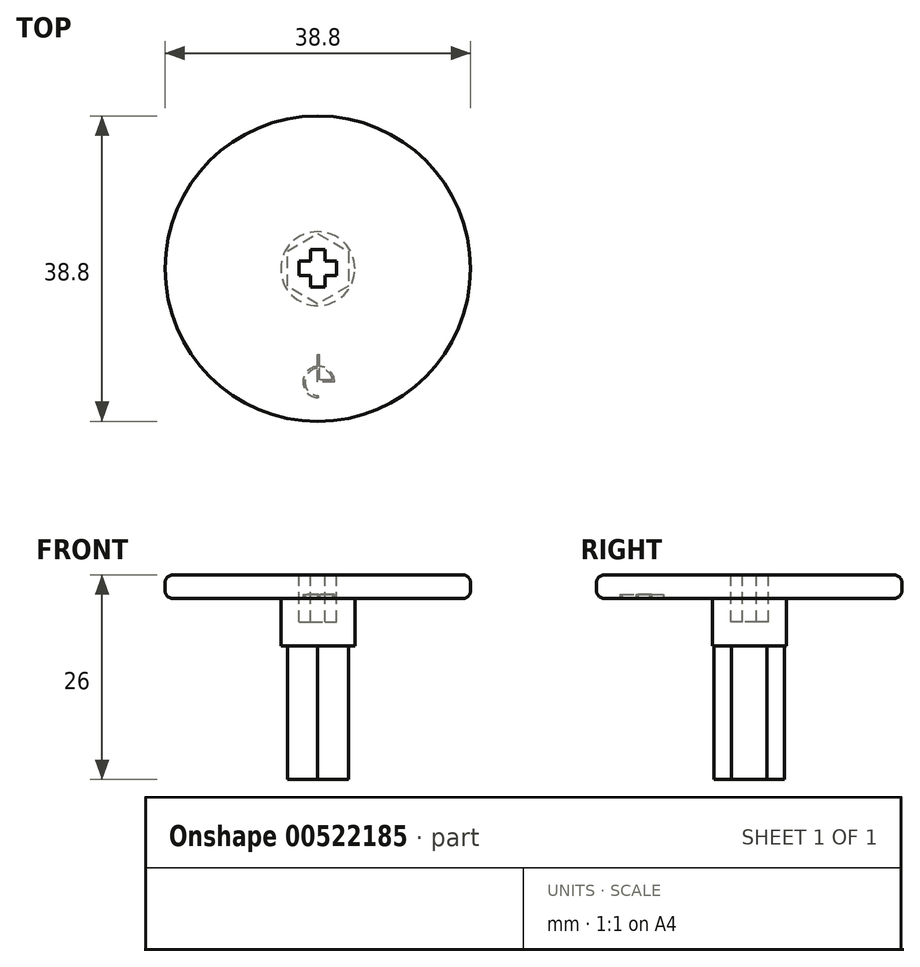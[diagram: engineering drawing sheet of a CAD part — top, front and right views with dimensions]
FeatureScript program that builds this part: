
annotation { "Feature Type Name" : "Feature", "Feature Type Description" : "" }
export const myFeature = defineFeature(function(context is Context, id is Id, definition is map)
    precondition{}
    {
        {
            var Q0;
            Q0=qCreatedBy(makeId("Top.planeOp"),FACE);
            var sketch = newSketch(context, id + "F0", { "sketchPlane" : qUnion([Q0])});
            skCircle(sketch, "E0.cCircle", {"center": v(0, 0) * mm, "radius": 3.88 * mm, "construction": true});
            skLineSegment(sketch, "E0.0", {"start": v(3.88, 2.24) * mm, "end": v(3.88, -2.24) * mm});
            skLineSegment(sketch, "E0.1", {"start": v(3.88, -2.24) * mm, "end": v(0, -4.47) * mm});
            skLineSegment(sketch, "E0.2", {"start": v(0, -4.47) * mm, "end": v(-3.87, -2.24) * mm});
            skLineSegment(sketch, "E0.3", {"start": v(-3.87, -2.24) * mm, "end": v(-3.88, 2.24) * mm});
            skLineSegment(sketch, "E0.4", {"start": v(-3.88, 2.24) * mm, "end": v(0, 4.47) * mm});
            skLineSegment(sketch, "E0.5", {"start": v(0, 4.47) * mm, "end": v(3.88, 2.24) * mm});
            skPoint(sketch, "E0.0.midPoint", {"position": v(3.88, 0) * mm});
            skSolve(sketch);
        }
        {
            var Q0;
            Q0=makeQuery(id+"F0.imprint","IMPRINT",FACE,{"disambiguationData":[TD([[makeQuery(id+"F0.imprint","IMPRINT",EDGE,{"derivedFrom":sQuery(id+"F0.wireOp",EDGE,"E0.0")}),-1.0]])]});
            extrude(context, id + "F1", {"entities" : qUnion([Q0]), "oppositeDirection" : true, "depth" : 17 * mm, "offsetDistance" : 25 * mm});
        }
        {
            var Q0;
            Q0=makeQuery(id+"F1.opExtrude","CAP_FACE",FACE,{"disambiguationData":[OSD([sQuery(id+"F0.wireOp",EDGE,"E0.0"),sQuery(id+"F0.wireOp",EDGE,"E0.1"),sQuery(id+"F0.wireOp",EDGE,"E0.2"),sQuery(id+"F0.wireOp",EDGE,"E0.3"),sQuery(id+"F0.wireOp",EDGE,"E0.4"),sQuery(id+"F0.wireOp",EDGE,"E0.5")])],"isStart":true});
            var sketch = newSketch(context, id + "F2", { "sketchPlane" : qUnion([Q0])});
            skCircle(sketch, "E1", {"center": v(0, 0) * mm, "radius": 4.7 * mm});
            skSolve(sketch);
        }
        {
            var Q0;
            Q0=qSketchRegion(id+"F2",true);
            extrude(context, id + "F3", {"entities" : qUnion([Q0]), "operationType" : NewBodyOperationType.ADD, "depth" : 6 * mm, "offsetDistance" : 25 * mm});
        }
        {
            var Q0;
            Q0=makeQuery(id+"F3.opExtrude","CAP_FACE",FACE,{"disambiguationData":[OSD([sQuery(id+"F2.wireOp",EDGE,"E1")])],"isStart":false});
            var sketch = newSketch(context, id + "F4", { "sketchPlane" : qUnion([Q0])});
            skCircle(sketch, "E2", {"center": v(0, 0) * mm, "radius": 19.4 * mm});
            skSolve(sketch);
        }
        {
            var Q0;
            Q0=qSketchRegion(id+"F4",true);
            extrude(context, id + "F5", {"entities" : qUnion([Q0]), "operationType" : NewBodyOperationType.ADD, "depth" : 3 * mm, "offsetDistance" : 25 * mm});
        }
        {
            var Q0;
            Q0=makeQuery(id+"F5.opExtrude","CAP_EDGE",EDGE,{"disambiguationData":[OSD([sQuery(id+"F4.wireOp",EDGE,"E2")])],"isStart":true});
            var Q1;
            Q1=makeQuery(id+"F5.opExtrude","CAP_EDGE",EDGE,{"disambiguationData":[OSD([sQuery(id+"F4.wireOp",EDGE,"E2")])],"isStart":false});
            fillet(context, id + "F6", {"entities" : qUnion([Q0, Q1]), "radius" : 1 * mm, "tangentPropagation" : true, "allowEdgeOverflow" : false});
        }
        {
            var Q0;
            Q0=makeQuery(id+"F5.opExtrude","CAP_FACE",FACE,{"disambiguationData":[OSD([sQuery(id+"F4.wireOp",EDGE,"E2")])],"isStart":false});
            var sketch = newSketch(context, id + "F7", { "sketchPlane" : qUnion([Q0])});
            skLineSegment(sketch, "E3.bottom", {"start": v(-0.9, 2.45) * mm, "end": v(0.9, 2.45) * mm});
            skLineSegment(sketch, "E3.top", {"start": v(-0.9, -2.35) * mm, "end": v(0.9, -2.35) * mm});
            skLineSegment(sketch, "E3.left", {"start": v(-0.9, 2.45) * mm, "end": v(-0.9, -2.35) * mm});
            skLineSegment(sketch, "E3.right", {"start": v(0.9, 2.45) * mm, "end": v(0.9, -2.35) * mm});
            skPoint(sketch, "E3.middle", {"position": v(0, 0.05) * mm});
            skLineSegment(sketch, "E4.bottom", {"start": v(-2.4, 0.95) * mm, "end": v(2.4, 0.95) * mm});
            skLineSegment(sketch, "E4.top", {"start": v(-2.4, -0.85) * mm, "end": v(2.4, -0.85) * mm});
            skLineSegment(sketch, "E4.left", {"start": v(-2.4, 0.95) * mm, "end": v(-2.4, -0.85) * mm});
            skLineSegment(sketch, "E4.right", {"start": v(2.4, 0.95) * mm, "end": v(2.4, -0.85) * mm});
            skSolve(sketch);
        }
        {
            var Q0;
            {var subQ5=sQuery(id+"F7.wireOp",EDGE,"E4.left");Q0=makeQuery(id+"F7.imprint","IMPRINT",FACE,{"disambiguationData":[TD([[makeQuery(id+"F7.imprint","IMPRINT",EDGE,{"derivedFrom":subQ5}),1.0]])]});}
            var Q1;
            {var subQ0=sQuery(id+"F7.wireOp",EDGE,"E3.bottom");Q1=makeQuery(id+"F7.imprint","IMPRINT",FACE,{"disambiguationData":[TD([[makeQuery(id+"F7.imprint","IMPRINT",EDGE,{"derivedFrom":subQ0}),-1.0]])]});}
            var Q2;
            {var subQ0=sQuery(id+"F7.wireOp",EDGE,"E4.bottom");var subQ1=sQuery(id+"F7.wireOp",EDGE,"E3.left");var subQ2=makeQuery(id+"F7.imprint","INTERSECT",VERTEX,{"derivedFrom":[subQ1,subQ0]});Q2=makeQuery(id+"F7.imprint","IMPRINT",FACE,{"disambiguationData":[TD([[makeQuery(id+"F7.imprint","IMPRINT",EDGE,{"disambiguationData":[TD([[subQ2,-1.0]])],"derivedFrom":subQ1}),1.0]])]});}
            var Q3;
            {var subQ5=sQuery(id+"F7.wireOp",EDGE,"E4.right");Q3=makeQuery(id+"F7.imprint","IMPRINT",FACE,{"disambiguationData":[TD([[makeQuery(id+"F7.imprint","IMPRINT",EDGE,{"derivedFrom":subQ5}),-1.0]])]});}
            var Q4;
            {var subQ0=sQuery(id+"F7.wireOp",EDGE,"E3.top");Q4=makeQuery(id+"F7.imprint","IMPRINT",FACE,{"disambiguationData":[TD([[makeQuery(id+"F7.imprint","IMPRINT",EDGE,{"derivedFrom":subQ0}),1.0]])]});}
            extrude(context, id + "F8", {"entities" : qUnion([Q0, Q1, Q2, Q3, Q4]), "operationType" : NewBodyOperationType.REMOVE, "oppositeDirection" : true, "depth" : 6 * mm, "offsetDistance" : 25 * mm});
        }
        {
            var Q0;
            Q0=makeQuery(id+"F5.opExtrude","CAP_FACE",FACE,{"disambiguationData":[OSD([sQuery(id+"F4.wireOp",EDGE,"E2")])],"isStart":true});
            var sketch = newSketch(context, id + "F9", { "sketchPlane" : qUnion([Q0])});
            skLineSegment(sketch, "E5.bottom", {"start": v(0.12, 16.4) * mm, "end": v(2.12, 16.4) * mm, "construction": true});
            skLineSegment(sketch, "E5.top", {"start": v(0.12, 14.4) * mm, "end": v(2.12, 14.4) * mm, "construction": true});
            skLineSegment(sketch, "E5.left", {"start": v(0.12, 16.4) * mm, "end": v(0.12, 14.4) * mm, "construction": true});
            skLineSegment(sketch, "E5.right", {"start": v(2.12, 16.4) * mm, "end": v(2.12, 14.4) * mm, "construction": true});
            skArc(sketch, "E6", {"start": v(0.12, 16.4) * mm, "mid": v(-1.3, 12.99) * mm, "end": v(2.12, 14.4) * mm});
            skLineSegment(sketch, "E7", {"start": v(0.12, 16.4) * mm, "end": v(0.12, 16.15) * mm});
            skLineSegment(sketch, "E8", {"start": v(2.12, 14.4) * mm, "end": v(1.87, 14.4) * mm});
            skArc(sketch, "E9", {"start": v(0.12, 16.15) * mm, "mid": v(-1.12, 13.16) * mm, "end": v(1.87, 14.4) * mm});
            skLineSegment(sketch, "E10", {"start": v(1.87, 14.4) * mm, "end": v(0, 14.4) * mm});
            skLineSegment(sketch, "E11", {"start": v(0, 14.4) * mm, "end": v(0, 10.9) * mm});
            skLineSegment(sketch, "E12", {"start": v(0, 10.9) * mm, "end": v(0.25, 10.9) * mm});
            skLineSegment(sketch, "E13", {"start": v(1.85, 14.15) * mm, "end": v(0.25, 14.15) * mm});
            skLineSegment(sketch, "E14", {"start": v(0.25, 14.15) * mm, "end": v(0.25, 10.9) * mm});
            skSolve(sketch);
        }
        {
            var Q0;
            Q0 = qSketchRegion(id + "F9", true);
            extrude(context, id + "F10", {"entities" : qUnion([Q0]), "operationType" : NewBodyOperationType.REMOVE, "oppositeDirection" : true, "depth" : .5 * mm, "offsetDistance" : 25 * mm});
        }
    });
